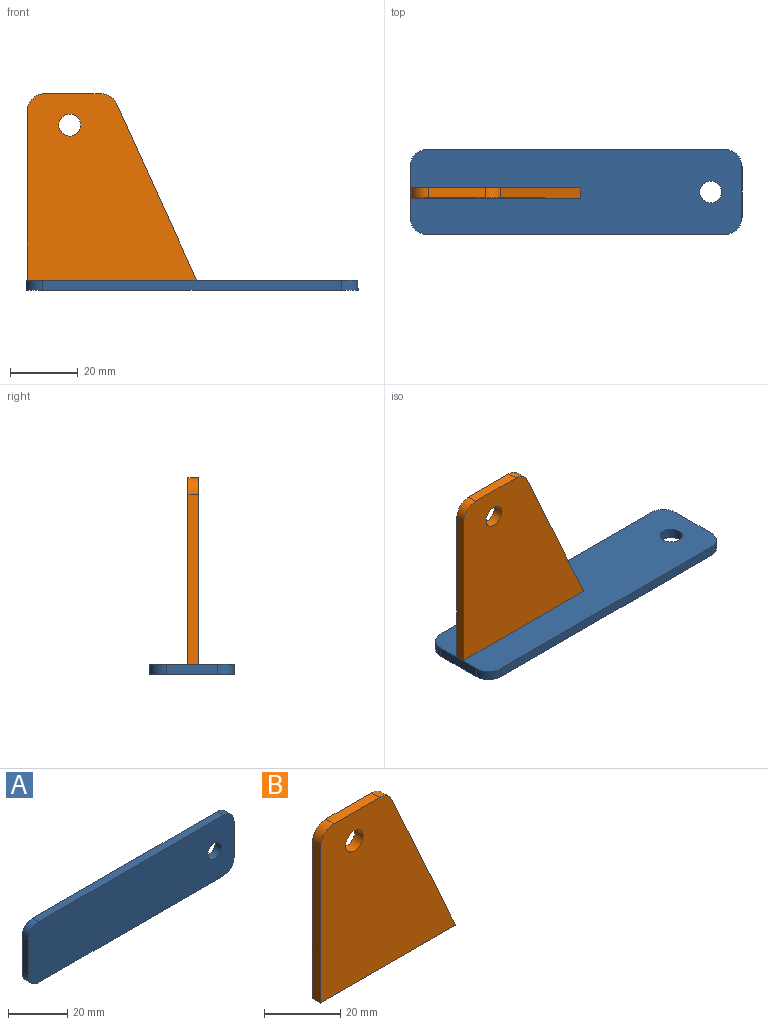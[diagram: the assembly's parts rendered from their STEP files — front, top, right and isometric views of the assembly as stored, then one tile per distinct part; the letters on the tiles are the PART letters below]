
ASSEMBLY  parts=2 mates=1
PART A: 11 faces, bbox 98x3x25 mm
  f0: cylinder r=5mm len=5mm, axis (0,1,0), area 23.6mm2, adj f1,f8,f9,f10
  f1: plane 88x3mm, normal (0,0,1), area 264mm2, adj f0,f2,f9,f10
  f2: cylinder r=5mm len=5mm, axis (0,1,0), area 23.6mm2, adj f1,f3,f9,f10
  f3: plane 15x3mm, normal (-1,0,0), area 45mm2, adj f2,f4,f9,f10
  f4: cylinder r=5mm len=5mm, axis (0,1,0), area 23.6mm2, adj f3,f5,f9,f10
  f5: plane 88x3mm, normal (0,0,-1), area 264mm2, adj f4,f6,f9,f10
  f6: cylinder r=5mm len=5mm, axis (0,1,0), area 23.6mm2, adj f5,f8,f9,f10
  f7: cylinder r=3.25mm len=6.5mm, axis (0,1,0), area 61.3mm2, adj f9,f10
  f8: plane 15x3mm, normal (1,0,0), area 45mm2, adj f0,f6,f9,f10
  f9: plane 98x25mm, normal (0,-1,0), area 2395.4mm2, adj f0,f1,f2,f3,f4,f5,f6,f7
  f10: plane 98x25mm, normal (0,1,0), area 2395.4mm2, adj f0,f1,f2,f3,f4,f5,f6,f7
PART B: 9 faces, bbox 50x3x55 mm
  f0: plane 50x3mm, normal (0,0,-1), area 150mm2, adj f1,f6,f7,f8
  f1: plane 52.07x23.67mm, normal (0.91,0,0.41), area 171.6mm2, adj f0,f2,f7,f8
  f2: cylinder r=5mm len=4.55mm, axis (0,1,0), area 17.2mm2, adj f1,f3,f7,f8
  f3: plane 16.78x3mm, normal (0,0,1), area 50.3mm2, adj f2,f4,f7,f8
  f4: cylinder r=5mm len=5mm, axis (0,1,0), area 23.6mm2, adj f3,f6,f7,f8
  f5: cylinder r=3.25mm len=6.5mm, axis (0,1,0), area 61.3mm2, adj f7,f8
  f6: plane 50x3mm, normal (-1,0,0), area 150mm2, adj f0,f4,f7,f8
  f7: plane 55x50mm, normal (0,-1,0), area 2022.2mm2, adj f0,f1,f2,f3,f4,f5,f6
  f8: plane 55x50mm, normal (0,1,0), area 2022.2mm2, adj f0,f1,f2,f3,f4,f5,f6
PLACE A rot(axis=(1,0,0),90deg) t=(-74.3,-12.35,-26.28)mm
PLACE B t=(-110.42,-11.17,1.22)mm
MATE planar B.f0 <-> A.f10  axis (0,0,-1) through (-97.92,-12.67,-26.28)mm
